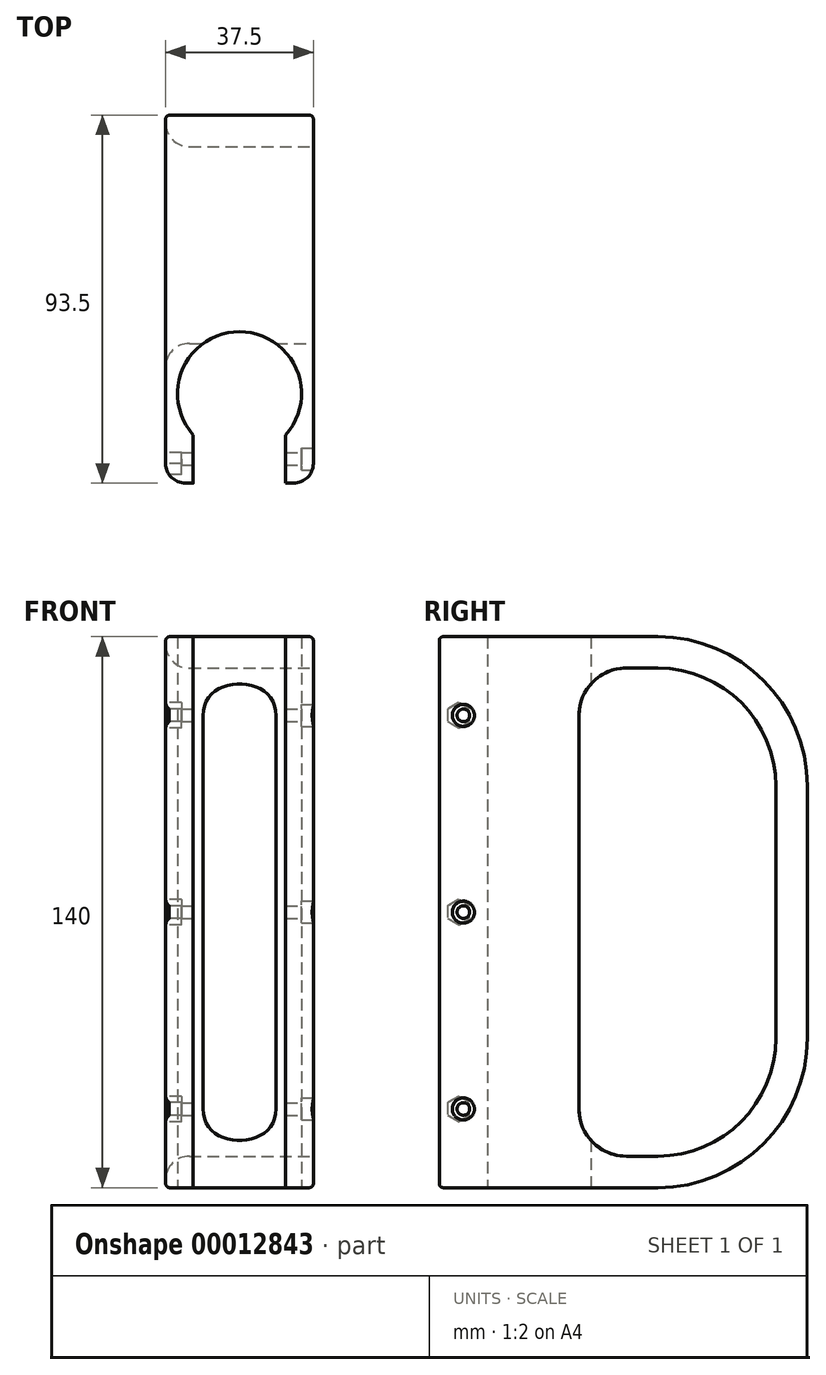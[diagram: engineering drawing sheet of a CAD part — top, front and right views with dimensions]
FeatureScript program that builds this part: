
annotation { "Feature Type Name" : "Feature", "Feature Type Description" : "" }
export const myFeature = defineFeature(function(context is Context, id is Id, definition is map)
    precondition{}
    {
        {
            var Q0;
            Q0=qCreatedBy(makeId("Top.planeOp"),FACE);
            var sketch = newSketch(context, id + "F0", { "sketchPlane" : qUnion([Q0])});
            skCircle(sketch, "E0", {"center": v(0, 0) * mm, "radius": 15.75 * mm});
            skSolve(sketch);
        }
        {
            var Q0;
            Q0=qCreatedBy(makeId("Top.planeOp"),FACE);
            var sketch = newSketch(context, id + "F1", { "sketchPlane" : qUnion([Q0])});
            skLineSegment(sketch, "E1", {"start": v(0, 70.75) * mm, "end": v(18.75, 70.75) * mm});
            skLineSegment(sketch, "E2", {"start": v(18.75, 70.75) * mm, "end": v(18.75, -22.75) * mm});
            skLineSegment(sketch, "E3", {"start": v(18.75, -22.75) * mm, "end": v(11.75, -22.75) * mm});
            skLineSegment(sketch, "E4", {"start": v(11.75, -22.75) * mm, "end": v(11.75, -10.49) * mm});
            skArc(sketch, "E5", {"start": v(11.75, -10.49) * mm, "mid": v(14.37, 6.44) * mm, "end": v(0, 15.75) * mm});
            skLineSegment(sketch, "E6", {"start": v(0, 15.75) * mm, "end": v(0, 70.75) * mm});
            skLineSegment(sketch, "E7", {"start": v(15.75, 0) * mm, "end": v(15.75, -22.75) * mm, "construction": true});
            skLineSegment(sketch, "E8", {"start": v(0, -15.75) * mm, "end": v(11.75, -15.75) * mm, "construction": true});
            skSolve(sketch);
        }
        {
            var Q0;
            Q0=makeQuery(id+"F1.imprint","IMPRINT",FACE,{"disambiguationData":[TD([[makeQuery(id+"F1.imprint","IMPRINT",EDGE,{"derivedFrom":sQuery(id+"F1.wireOp",EDGE,"E1")}),-1.0]])]});
            extrude(context, id + "F2", {"entities" : qUnion([Q0]), "depth" : 70 * mm});
        }
        {
            var Q0;
            Q0=makeQuery(id+"F2.opExtrude","SWEPT_BODY",BODY,{"disambiguationData":[OSD([sQuery(id+"F1.wireOp",EDGE,"E1"),sQuery(id+"F1.wireOp",EDGE,"E2"),sQuery(id+"F1.wireOp",EDGE,"E3"),sQuery(id+"F1.wireOp",EDGE,"E4"),sQuery(id+"F1.wireOp",EDGE,"E5"),sQuery(id+"F1.wireOp",EDGE,"E6")])]});
            var Q1;
            Q1=makeQuery(id+"F2.opExtrude","SWEPT_FACE",FACE,{"disambiguationData":[OSD([sQuery(id+"F1.wireOp",EDGE,"E6")])]});
            mirror(context, id + "F3", {"operationType" : NewBodyOperationType.ADD, "entities" : qUnion([Q0]), "mirrorPlane" : qUnion([Q1])});
        }
        {
            var Q0;
            Q0=makeQuery(id+"F2.opExtrude","SWEPT_FACE",FACE,{"disambiguationData":[OSD([sQuery(id+"F1.wireOp",EDGE,"E2")])]});
            var sketch = newSketch(context, id + "F4", { "sketchPlane" : qUnion([Q0])});
            skLineSegment(sketch, "E9", {"start": v(62.75, 70) * mm, "end": v(62.75, 38) * mm});
            skLineSegment(sketch, "E10", {"start": v(12.75, 20) * mm, "end": v(12.75, 70) * mm});
            skLineSegment(sketch, "E11", {"start": v(62.75, 70) * mm, "end": v(12.75, 70) * mm});
            skLineSegment(sketch, "E12", {"start": v(15.75, 70) * mm, "end": v(15.75, 0) * mm, "construction": true});
            skLineSegment(sketch, "E13", {"start": v(70.75, 8) * mm, "end": v(15.75, 8) * mm, "construction": true});
            skLineSegment(sketch, "E14", {"start": v(32.75, 8) * mm, "end": v(24.75, 8) * mm});
            skArc(sketch, "E15", {"start": v(12.75, 20) * mm, "mid": v(16.26, 11.51) * mm, "end": v(24.75, 8) * mm});
            skArc(sketch, "E16", {"start": v(32.75, 8) * mm, "mid": v(53.96, 16.79) * mm, "end": v(62.75, 38) * mm});
            skSolve(sketch);
        }
        {
            var Q0;
            Q0 = qSketchRegion(id + "F4", true);
            var Q1;
            {var subQ2=sQuery(id+"F4.wireOp",EDGE,"E11");Q1=makeQuery(id+"F4.imprint","IMPRINT",FACE,{"disambiguationData":[TD([[makeQuery(id+"F4.imprint","IMPRINT",EDGE,{"derivedFrom":subQ2}),1.0]])]});}
            extrude(context, id + "F5", {"entities" : qUnion([Q0, Q1]), "operationType" : NewBodyOperationType.REMOVE, "endBound" : BoundingType.THROUGH_ALL, "oppositeDirection" : true, "depth" : 25 * mm});
        }
        {
            var Q0;
            {var subQ0=makeQuery(id+"F2.opExtrude","SWEPT_FACE",FACE,{"disambiguationData":[OSD([sQuery(id+"F1.wireOp",EDGE,"E2")])]});Q0=makeQuery(id+"F8.boolean.opBoolean","MERGE",FACE,{"derivedFrom":[subQ0,makeQuery(id+"F8.opPattern","COPY",FACE,{"derivedFrom":subQ0,"instanceName":"1"})]});}
            var sketch = newSketch(context, id + "F6", { "sketchPlane" : qUnion([Q0])});
            skArc(sketch, "E17", {"start": v(32.75, 0) * mm, "mid": v(59.62, 11.13) * mm, "end": v(70.75, 38) * mm});
            skLineSegment(sketch, "E18", {"start": v(70.75, 38) * mm, "end": v(70.75, 0) * mm});
            skLineSegment(sketch, "E19", {"start": v(70.75, 0) * mm, "end": v(32.75, 0) * mm});
            skSolve(sketch);
        }
        {
            var Q0;
            Q0 = qSketchRegion(id + "F6", true);
            extrude(context, id + "F7", {"entities" : qUnion([Q0]), "operationType" : NewBodyOperationType.REMOVE, "endBound" : BoundingType.THROUGH_ALL, "oppositeDirection" : true, "depth" : 25 * mm});
        }
        {
            var Q0;
            Q0=makeQuery(id+"F2.opExtrude","SWEPT_BODY",BODY,{"disambiguationData":[OSD([sQuery(id+"F1.wireOp",EDGE,"E1"),sQuery(id+"F1.wireOp",EDGE,"E2"),sQuery(id+"F1.wireOp",EDGE,"E3"),sQuery(id+"F1.wireOp",EDGE,"E4"),sQuery(id+"F1.wireOp",EDGE,"E5"),sQuery(id+"F1.wireOp",EDGE,"E6")])]});
            var Q1;
            {var subQ0=sQuery(id+"F1.wireOp",EDGE,"E2");var subQ1=sQuery(id+"F1.wireOp",EDGE,"E3");var subQ2=sQuery(id+"F1.wireOp",EDGE,"E4");var subQ3=sQuery(id+"F1.wireOp",EDGE,"E5");var subQ4=makeQuery(id+"F2.opExtrude","CAP_FACE",FACE,{"disambiguationData":[OSD([sQuery(id+"F1.wireOp",EDGE,"E1"),subQ0,subQ1,subQ2,subQ3,sQuery(id+"F1.wireOp",EDGE,"E6")])],"isStart":false});var subQ6=makeQuery(id+"F2.opExtrude","SWEPT_FACE",FACE,{"disambiguationData":[OSD([subQ1])]});Q1=makeQuery(id+"F5.boolean.opBoolean","SPLIT",FACE,{"disambiguationData":[TD([subQ6])],"derivedFrom":makeQuery(id+"F3.boolean.opBoolean","MERGE",FACE,{"derivedFrom":[subQ4,makeQuery(id+"F3.opPattern","COPY",FACE,{"derivedFrom":subQ4,"instanceName":"1"})]})});}
            mirror(context, id + "F8", {"operationType" : NewBodyOperationType.ADD, "entities" : qUnion([Q0]), "mirrorPlane" : qUnion([Q1])});
        }
        {
            var Q0;
            {var subQ0=makeQuery(id+"F5.boolean.opBoolean","COPY",EDGE,{"derivedFrom":makeQuery(id+"F5.opExtrude","CAP_EDGE",EDGE,{"disambiguationData":[OSD([sQuery(id+"F4.wireOp",EDGE,"E10")])],"isStart":true})});Q0=makeQuery(id+"F8.boolean.opBoolean","MERGE",EDGE,{"derivedFrom":[subQ0,makeQuery(id+"F8.opPattern","COPY",EDGE,{"derivedFrom":subQ0,"instanceName":"1"})]});}
            var Q1;
            {var subQ0=makeQuery(id+"F5.boolean.opBoolean","INTERSECT",EDGE,{"derivedFrom":[makeQuery(id+"F3.opPattern","COPY",FACE,{"derivedFrom":makeQuery(id+"F2.opExtrude","SWEPT_FACE",FACE,{"disambiguationData":[OSD([sQuery(id+"F1.wireOp",EDGE,"E2")])]}),"instanceName":"1"}),makeQuery(id+"F5.opExtrude","SWEPT_FACE",FACE,{"disambiguationData":[OSD([sQuery(id+"F4.wireOp",EDGE,"E10")])]})]});Q1=makeQuery(id+"F8.boolean.opBoolean","MERGE",EDGE,{"derivedFrom":[subQ0,makeQuery(id+"F8.opPattern","COPY",EDGE,{"derivedFrom":subQ0,"instanceName":"1"})]});}
            fillet(context, id + "F9", {"entities" : qUnion([Q0, Q1]), "radius" : 6 * mm, "tangentPropagation" : true, "allowEdgeOverflow" : false});
        }
        {
            var Q0;
            {var subQ0=makeQuery(id+"F2.opExtrude","SWEPT_FACE",FACE,{"disambiguationData":[OSD([sQuery(id+"F1.wireOp",EDGE,"E2")])]});Q0=makeQuery(id+"F8.boolean.opBoolean","MERGE",FACE,{"derivedFrom":[subQ0,makeQuery(id+"F8.opPattern","COPY",FACE,{"derivedFrom":subQ0,"instanceName":"1"})]});}
            var sketch = newSketch(context, id + "F10", { "sketchPlane" : qUnion([Q0])});
            skCircle(sketch, "E20", {"center": v(-16.62, 20) * mm, "radius": 1.6 * mm});
            skCircle(sketch, "E21", {"center": v(-16.62, 70) * mm, "radius": 1.6 * mm});
            skCircle(sketch, "E22", {"center": v(-16.62, 120) * mm, "radius": 1.6 * mm});
            skLineSegment(sketch, "E23", {"start": v(-16.62, 20) * mm, "end": v(-16.62, 70) * mm, "construction": true});
            skLineSegment(sketch, "E24", {"start": v(-16.62, 70) * mm, "end": v(-16.62, 120) * mm, "construction": true});
            skLineSegment(sketch, "E25", {"start": v(-16.62, 120) * mm, "end": v(-16.62, 140) * mm, "construction": true});
            skLineSegment(sketch, "E26", {"start": v(-16.62, 20) * mm, "end": v(-16.62, 0) * mm, "construction": true});
            skSolve(sketch);
        }
        {
            var Q0;
            Q0 = qSketchRegion(id + "F10", true);
            extrude(context, id + "F11", {"entities" : qUnion([Q0]), "operationType" : NewBodyOperationType.REMOVE, "endBound" : BoundingType.THROUGH_ALL, "oppositeDirection" : true, "depth" : 25 * mm});
        }
        {
            var Q0;
            {var subQ0=makeQuery(id+"F2.opExtrude","SWEPT_FACE",FACE,{"disambiguationData":[OSD([sQuery(id+"F1.wireOp",EDGE,"E2")])]});Q0=makeQuery(id+"F8.boolean.opBoolean","MERGE",FACE,{"derivedFrom":[subQ0,makeQuery(id+"F8.opPattern","COPY",FACE,{"derivedFrom":subQ0,"instanceName":"1"})]});}
            var sketch = newSketch(context, id + "F12", { "sketchPlane" : qUnion([Q0])});
            skCircle(sketch, "E27", {"center": v(-16.62, 120) * mm, "radius": 2.8 * mm});
            skCircle(sketch, "E28", {"center": v(-16.62, 70) * mm, "radius": 2.8 * mm});
            skCircle(sketch, "E29", {"center": v(-16.62, 20) * mm, "radius": 2.8 * mm});
            skSolve(sketch);
        }
        {
            var Q0;
            Q0 = qSketchRegion(id + "F12", true);
            extrude(context, id + "F13", {"entities" : qUnion([Q0]), "operationType" : NewBodyOperationType.REMOVE, "oppositeDirection" : true, "depth" : 3 * mm});
        }
        {
            var Q0;
            {var subQ0=makeQuery(id+"F3.opPattern","COPY",FACE,{"derivedFrom":makeQuery(id+"F2.opExtrude","SWEPT_FACE",FACE,{"disambiguationData":[OSD([sQuery(id+"F1.wireOp",EDGE,"E2")])]}),"instanceName":"1"});Q0=makeQuery(id+"F8.boolean.opBoolean","MERGE",FACE,{"derivedFrom":[subQ0,makeQuery(id+"F8.opPattern","COPY",FACE,{"derivedFrom":subQ0,"instanceName":"1"})]});}
            var sketch = newSketch(context, id + "F14", { "sketchPlane" : qUnion([Q0])});
            skLineSegment(sketch, "E30", {"start": v(15, 68.38) * mm, "end": v(15, 71.62) * mm});
            skLineSegment(sketch, "E31", {"start": v(15, 71.62) * mm, "end": v(17.8, 73.23) * mm});
            skLineSegment(sketch, "E32", {"start": v(17.8, 73.23) * mm, "end": v(20.6, 71.62) * mm});
            skLineSegment(sketch, "E33", {"start": v(20.6, 71.62) * mm, "end": v(20.6, 68.38) * mm});
            skLineSegment(sketch, "E34", {"start": v(20.6, 68.38) * mm, "end": v(17.8, 66.77) * mm});
            skLineSegment(sketch, "E35", {"start": v(17.8, 66.77) * mm, "end": v(15, 68.38) * mm});
            skLineSegment(sketch, "E36", {"start": v(15, 118.38) * mm, "end": v(15, 121.62) * mm});
            skLineSegment(sketch, "E37", {"start": v(15, 121.62) * mm, "end": v(17.8, 123.23) * mm});
            skLineSegment(sketch, "E38", {"start": v(17.8, 123.23) * mm, "end": v(20.6, 121.62) * mm});
            skLineSegment(sketch, "E39", {"start": v(20.6, 121.62) * mm, "end": v(20.6, 118.38) * mm});
            skLineSegment(sketch, "E40", {"start": v(20.6, 118.38) * mm, "end": v(17.8, 116.77) * mm});
            skLineSegment(sketch, "E41", {"start": v(17.8, 116.77) * mm, "end": v(15, 118.38) * mm});
            skLineSegment(sketch, "E42", {"start": v(15, 18.38) * mm, "end": v(15, 21.62) * mm});
            skLineSegment(sketch, "E43", {"start": v(15, 21.62) * mm, "end": v(17.8, 23.23) * mm});
            skLineSegment(sketch, "E44", {"start": v(17.8, 23.23) * mm, "end": v(20.6, 21.62) * mm});
            skLineSegment(sketch, "E45", {"start": v(20.6, 21.62) * mm, "end": v(20.6, 18.38) * mm});
            skLineSegment(sketch, "E46", {"start": v(20.6, 18.38) * mm, "end": v(17.8, 16.77) * mm});
            skLineSegment(sketch, "E47", {"start": v(17.8, 16.77) * mm, "end": v(15, 18.38) * mm});
            skCircle(sketch, "E48", {"center": v(17.8, 20) * mm, "radius": 3.23 * mm, "construction": true});
            skCircle(sketch, "E49", {"center": v(17.8, 70) * mm, "radius": 3.23 * mm, "construction": true});
            skCircle(sketch, "E50", {"center": v(17.8, 120) * mm, "radius": 3.23 * mm, "construction": true});
            skSolve(sketch);
        }
        {
            var Q0;
            Q0=makeQuery(id+"F14.imprint","IMPRINT",FACE,{"disambiguationData":[TD([[makeQuery(id+"F14.imprint","IMPRINT",EDGE,{"derivedFrom":sQuery(id+"F14.wireOp",EDGE,"E42")}),-1.0]])]});
            var Q1;
            Q1=makeQuery(id+"F14.imprint","IMPRINT",FACE,{"disambiguationData":[TD([[makeQuery(id+"F14.imprint","IMPRINT",EDGE,{"derivedFrom":sQuery(id+"F14.wireOp",EDGE,"E30")}),-1.0]])]});
            var Q2;
            Q2=makeQuery(id+"F14.imprint","IMPRINT",FACE,{"disambiguationData":[TD([[makeQuery(id+"F14.imprint","IMPRINT",EDGE,{"derivedFrom":sQuery(id+"F14.wireOp",EDGE,"E36")}),-1.0]])]});
            extrude(context, id + "F15", {"entities" : qUnion([Q0, Q1, Q2]), "operationType" : NewBodyOperationType.REMOVE, "oppositeDirection" : true, "depth" : 4 * mm});
        }
        {
            var Q0;
            {var subQ0=makeQuery(id+"F2.opExtrude","SWEPT_EDGE",EDGE,{"disambiguationData":[OSD([sQuery(id+"F1.wireOp",EDGE,"E2"),sQuery(id+"F1.wireOp",EDGE,"E3")])]});Q0=makeQuery(id+"F8.boolean.opBoolean","MERGE",EDGE,{"derivedFrom":[subQ0,makeQuery(id+"F8.opPattern","COPY",EDGE,{"derivedFrom":subQ0,"instanceName":"1"})]});}
            var Q1;
            {var subQ0=makeQuery(id+"F3.opPattern","COPY",EDGE,{"derivedFrom":makeQuery(id+"F2.opExtrude","SWEPT_EDGE",EDGE,{"disambiguationData":[OSD([sQuery(id+"F1.wireOp",EDGE,"E2"),sQuery(id+"F1.wireOp",EDGE,"E3")])]}),"instanceName":"1"});Q1=makeQuery(id+"F8.boolean.opBoolean","MERGE",EDGE,{"derivedFrom":[subQ0,makeQuery(id+"F8.opPattern","COPY",EDGE,{"derivedFrom":subQ0,"instanceName":"1"})]});}
            fillet(context, id + "F16", {"entities" : qUnion([Q0, Q1]), "radius" : 5 * mm, "tangentPropagation" : true, "allowEdgeOverflow" : false});
        }
        {
            var Q0;
            Q0=makeQuery(id+"F3.opPattern","COPY",EDGE,{"derivedFrom":makeQuery(id+"F2.opExtrude","CAP_EDGE",EDGE,{"disambiguationData":[OSD([sQuery(id+"F1.wireOp",EDGE,"E2")])],"isStart":true}),"instanceName":"1"});
            var Q1;
            {var subQ0=makeQuery(id+"F5.boolean.opBoolean","INTERSECT",EDGE,{"derivedFrom":[makeQuery(id+"F3.opPattern","COPY",FACE,{"derivedFrom":makeQuery(id+"F2.opExtrude","SWEPT_FACE",FACE,{"disambiguationData":[OSD([sQuery(id+"F1.wireOp",EDGE,"E2")])]}),"instanceName":"1"}),makeQuery(id+"F5.opExtrude","SWEPT_FACE",FACE,{"disambiguationData":[OSD([sQuery(id+"F4.wireOp",EDGE,"E9")])]})]});var subQ1=makeQuery(id+"F2.opExtrude","SWEPT_FACE",FACE,{"disambiguationData":[OSD([sQuery(id+"F1.wireOp",EDGE,"E1")])]});var subQ2=makeQuery(id+"F3.boolean.opBoolean","MERGE",FACE,{"derivedFrom":[subQ1,makeQuery(id+"F3.opPattern","COPY",FACE,{"derivedFrom":subQ1,"instanceName":"1"})]});Q1=makeQuery(id+"F9.opFillet","BLEND_EDGE",EDGE,{"blendedFrom":[makeQuery(id+"F8.boolean.opBoolean","MERGE",EDGE,{"derivedFrom":[subQ0,makeQuery(id+"F8.opPattern","COPY",EDGE,{"derivedFrom":subQ0,"instanceName":"1"})]}),makeQuery(id+"F8.boolean.opBoolean","MERGE",FACE,{"derivedFrom":[subQ2,makeQuery(id+"F8.opPattern","COPY",FACE,{"derivedFrom":subQ2,"instanceName":"1"})]})],"blendedInto":[makeQuery(id+"F8.boolean.opBoolean","MERGE",FACE,{"derivedFrom":[subQ2,makeQuery(id+"F8.opPattern","COPY",FACE,{"derivedFrom":subQ2,"instanceName":"1"})]})]});}
            var Q2;
            Q2=makeQuery(id+"F8.opPattern","COPY",EDGE,{"derivedFrom":makeQuery(id+"F2.opExtrude","CAP_EDGE",EDGE,{"disambiguationData":[OSD([sQuery(id+"F1.wireOp",EDGE,"E2")])],"isStart":true}),"instanceName":"1"});
            fillet(context, id + "F17", {"entities" : qUnion([Q0, Q1, Q2]), "radius" : 1 * mm, "tangentPropagation" : true, "allowEdgeOverflow" : false});
        }
    });
